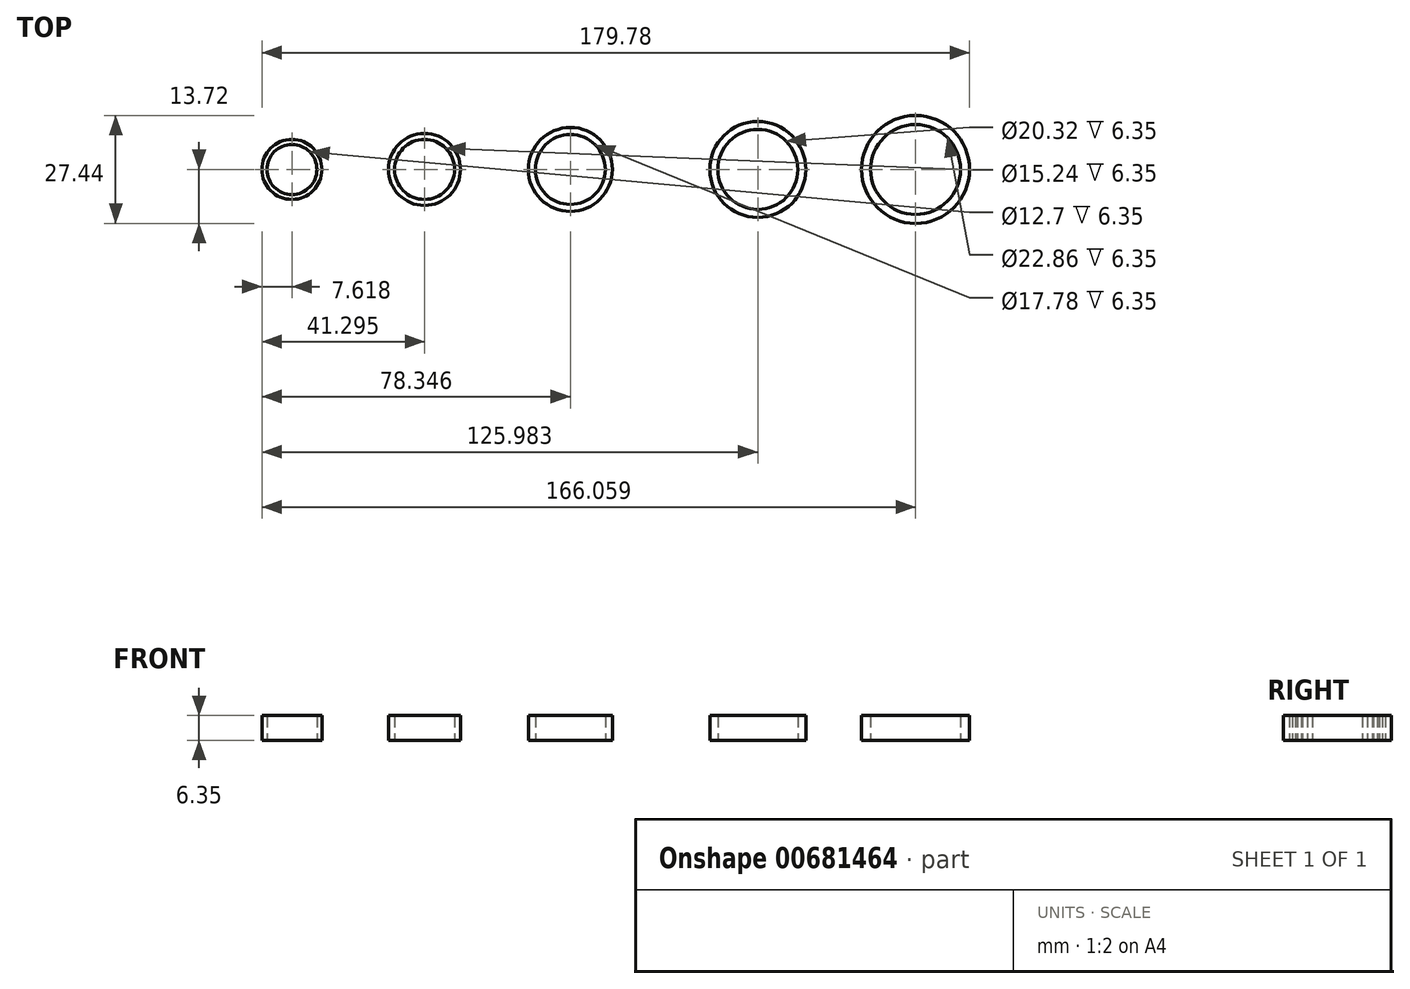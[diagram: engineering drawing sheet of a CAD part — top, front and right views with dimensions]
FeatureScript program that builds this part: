
annotation { "Feature Type Name" : "Feature", "Feature Type Description" : "" }
export const myFeature = defineFeature(function(context is Context, id is Id, definition is map)
    precondition{}
    {
        {
            var Q0;
            Q0=qCreatedBy(makeId("Top.planeOp"),FACE);
            var sketch = newSketch(context, id + "F0", { "sketchPlane" : qUnion([Q0])});
            skLineSegment(sketch, "E0", {"start": v(-117.53, 0) * mm, "end": v(134.27, 0) * mm, "construction": true});
            skCircle(sketch, "E1", {"center": v(-103.54, 0) * mm, "radius": 6.35 * mm});
            skCircle(sketch, "E2", {"center": v(-103.54, 0) * mm, "radius": 7.62 * mm});
            skCircle(sketch, "E3", {"center": v(-69.87, 0) * mm, "radius": 7.62 * mm});
            skCircle(sketch, "E4", {"center": v(-69.87, 0) * mm, "radius": 9.14 * mm});
            skCircle(sketch, "E5", {"center": v(-32.81, 0) * mm, "radius": 8.9 * mm});
            skCircle(sketch, "E6", {"center": v(-32.81, 0) * mm, "radius": 10.67 * mm});
            skCircle(sketch, "E7", {"center": v(14.82, 0) * mm, "radius": 10.16 * mm});
            skCircle(sketch, "E8", {"center": v(14.82, 0) * mm, "radius": 12.2 * mm});
            skCircle(sketch, "E9", {"center": v(54.9, 0) * mm, "radius": 11.43 * mm});
            skCircle(sketch, "E10", {"center": v(54.9, 0) * mm, "radius": 13.72 * mm});
            skSolve(sketch);
        }
        {
            var Q0;
            Q0 = qSketchRegion(id + "F0", true);
            extrude(context, id + "F1", {"entities" : qUnion([Q0]), "depth" : 6.35 * mm, "offsetDistance" : 25.4 * mm});
        }
    });
